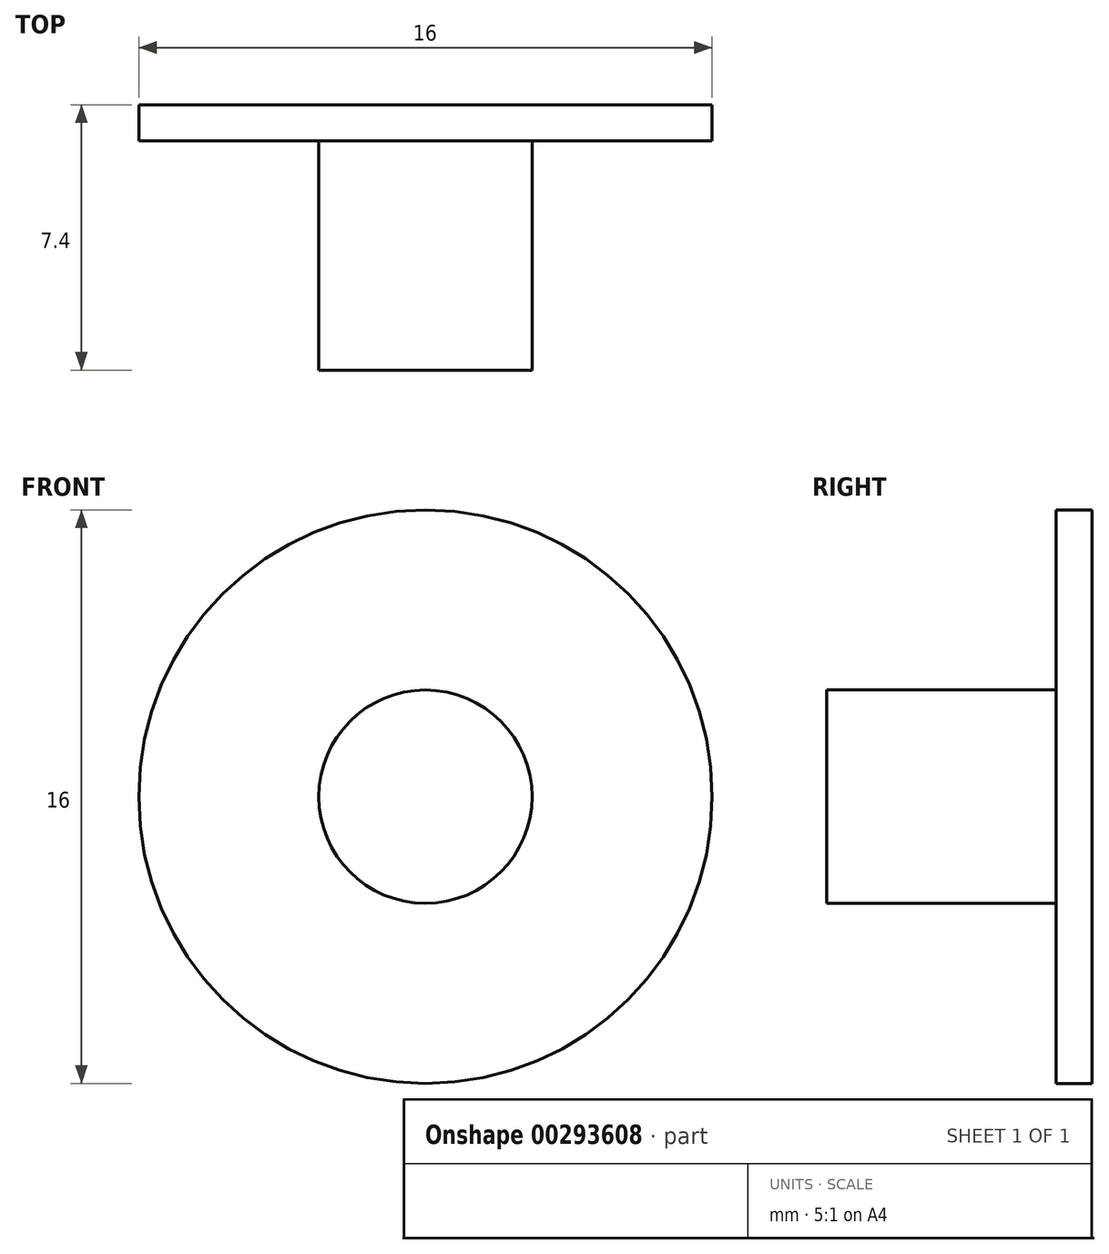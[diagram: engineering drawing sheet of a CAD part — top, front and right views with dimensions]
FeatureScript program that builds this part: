
annotation { "Feature Type Name" : "Feature", "Feature Type Description" : "" }
export const myFeature = defineFeature(function(context is Context, id is Id, definition is map)
    precondition{}
    {
        {
            var Q0;
            Q0=qCreatedBy(makeId("Front.planeOp"),FACE);
            var sketch = newSketch(context, id + "F0", { "sketchPlane" : qUnion([Q0])});
            skCircle(sketch, "E0", {"center": v(0, 0) * mm, "radius": 2.98 * mm});
            skSolve(sketch);
        }
        {
            var Q0;
            Q0 = qSketchRegion(id + "F0", true);
            extrude(context, id + "F1", {"entities" : qUnion([Q0]), "depth" : 7.4 * mm});
        }
        {
            var Q0;
            Q0=qCreatedBy(makeId("Front.planeOp"),FACE);
            var sketch = newSketch(context, id + "F2", { "sketchPlane" : qUnion([Q0])});
            skCircle(sketch, "E1", {"center": v(0, 0) * mm, "radius": 8 * mm});
            skSolve(sketch);
        }
        {
            var Q0;
            Q0=makeQuery(id+"F2.imprint","IMPRINT",FACE,{"disambiguationData":[TD([[makeQuery(id+"F2.imprint","IMPRINT",EDGE,{"derivedFrom":sQuery(id+"F2.wireOp",EDGE,"E1")}),1.0]])]});
            extrude(context, id + "F3", {"entities" : qUnion([Q0]), "operationType" : NewBodyOperationType.ADD, "depth" : 1 * mm});
        }
    });
